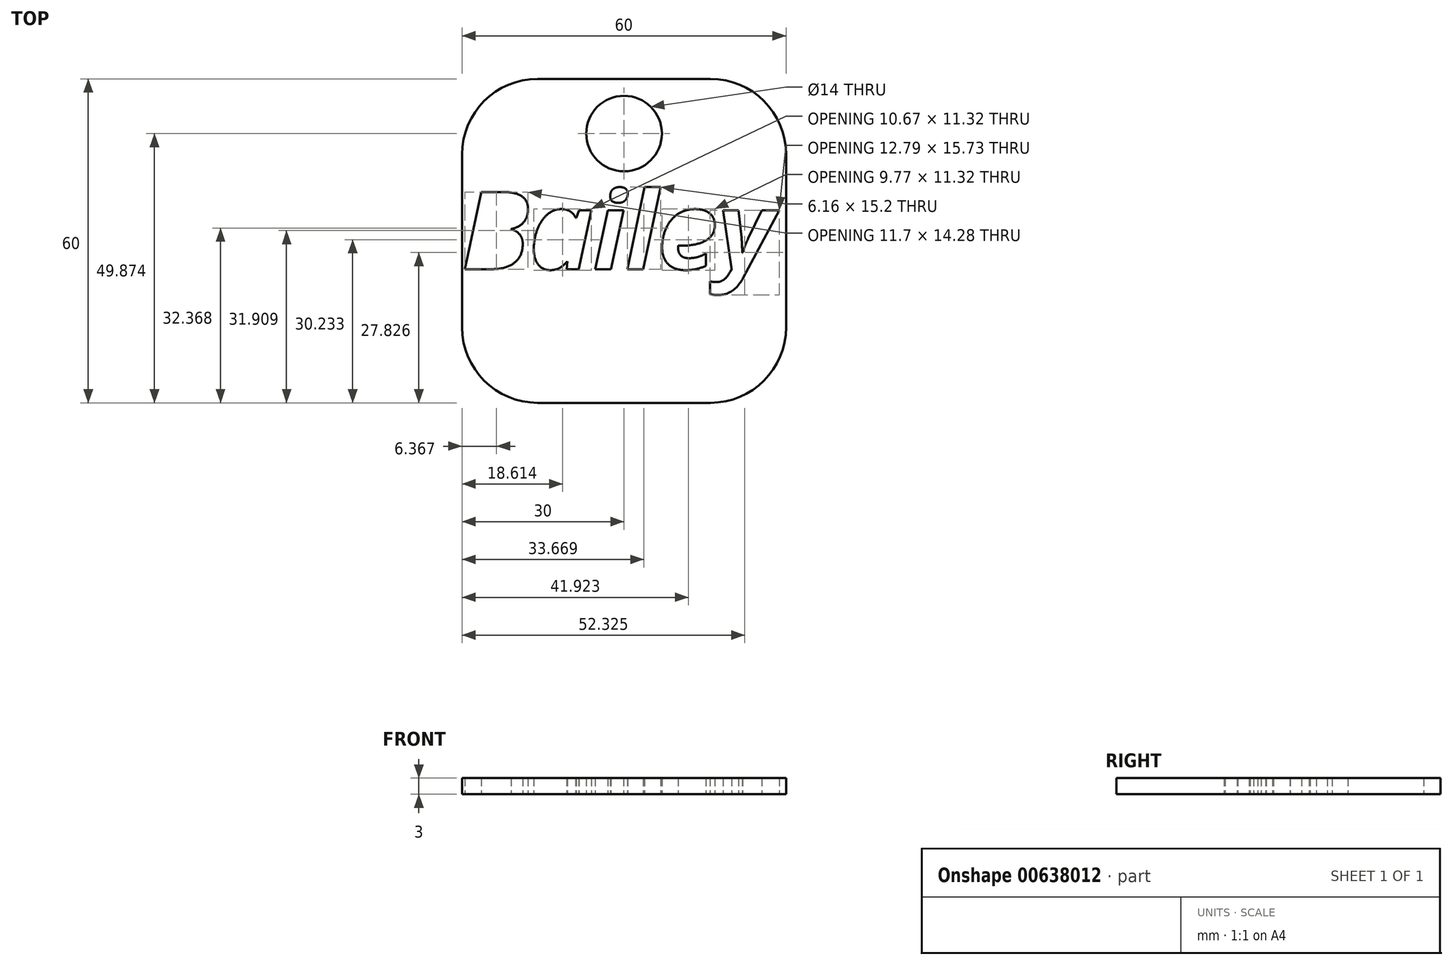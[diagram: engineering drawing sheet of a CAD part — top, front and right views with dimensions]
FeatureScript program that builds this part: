
annotation { "Feature Type Name" : "Feature", "Feature Type Description" : "" }
export const myFeature = defineFeature(function(context is Context, id is Id, definition is map)
    precondition{}
    {
        {
            var Q0;
            Q0=qCreatedBy(makeId("Top.planeOp"),FACE);
            var sketch = newSketch(context, id + "F0", { "sketchPlane" : qUnion([Q0])});
            skLineSegment(sketch, "E0.bottom", {"start": v(16, 30) * mm, "end": v(-16, 30) * mm});
            skLineSegment(sketch, "E0.top", {"start": v(16, -30) * mm, "end": v(-16, -30) * mm});
            skLineSegment(sketch, "E0.left", {"start": v(30, 16) * mm, "end": v(30, -16) * mm});
            skLineSegment(sketch, "E0.right", {"start": v(-30, 16) * mm, "end": v(-30, -16) * mm});
            skPoint(sketch, "E0.middle", {"position": v(0, 0) * mm});
            skText(sketch, "E1", { "text": "Bailey", "fontName": "OpenSans-BoldItalic.ttf"});
            skPoint(sketch, "E2.visualSharp", {"position": v(-30, 30) * mm});
            skArc(sketch, "E2.filletArc", {"start": v(-16, 30) * mm, "mid": v(-25.9, 25.9) * mm, "end": v(-30, 16) * mm});
            skPoint(sketch, "E3.visualSharp", {"position": v(30, 30) * mm});
            skArc(sketch, "E3.filletArc", {"start": v(30, 16) * mm, "mid": v(25.9, 25.9) * mm, "end": v(16, 30) * mm});
            skPoint(sketch, "E4.visualSharp", {"position": v(30, -30) * mm});
            skArc(sketch, "E4.filletArc", {"start": v(16, -30) * mm, "mid": v(25.9, -25.9) * mm, "end": v(30, -16) * mm});
            skPoint(sketch, "E5.visualSharp", {"position": v(-30, -30) * mm});
            skArc(sketch, "E5.filletArc", {"start": v(-30, -16) * mm, "mid": v(-25.9, -25.9) * mm, "end": v(-16, -30) * mm});
            skCircle(sketch, "E6", {"center": v(0, 19.87) * mm, "radius": 7 * mm});
            const initialGuessF0  = {"E1": [-0.03, -0.00523, 1, 0, 0.0144]};
            skSetInitialGuess(sketch, initialGuessF0);
            skSolve(sketch);
        }
        {
            var Q0;
            Q0=makeQuery(id+"F0.imprint","IMPRINT",FACE,{"disambiguationData":[TD([[makeQuery(id+"F0.imprint","IMPRINT",EDGE,{"derivedFrom":sQuery(id+"F0.wireOp",EDGE,"E0.bottom")}),1.0]])]});
            extrude(context, id + "F1", {"entities" : qUnion([Q0]), "depth" : 3 * mm, "offsetDistance" : 25 * mm});
        }
    });
